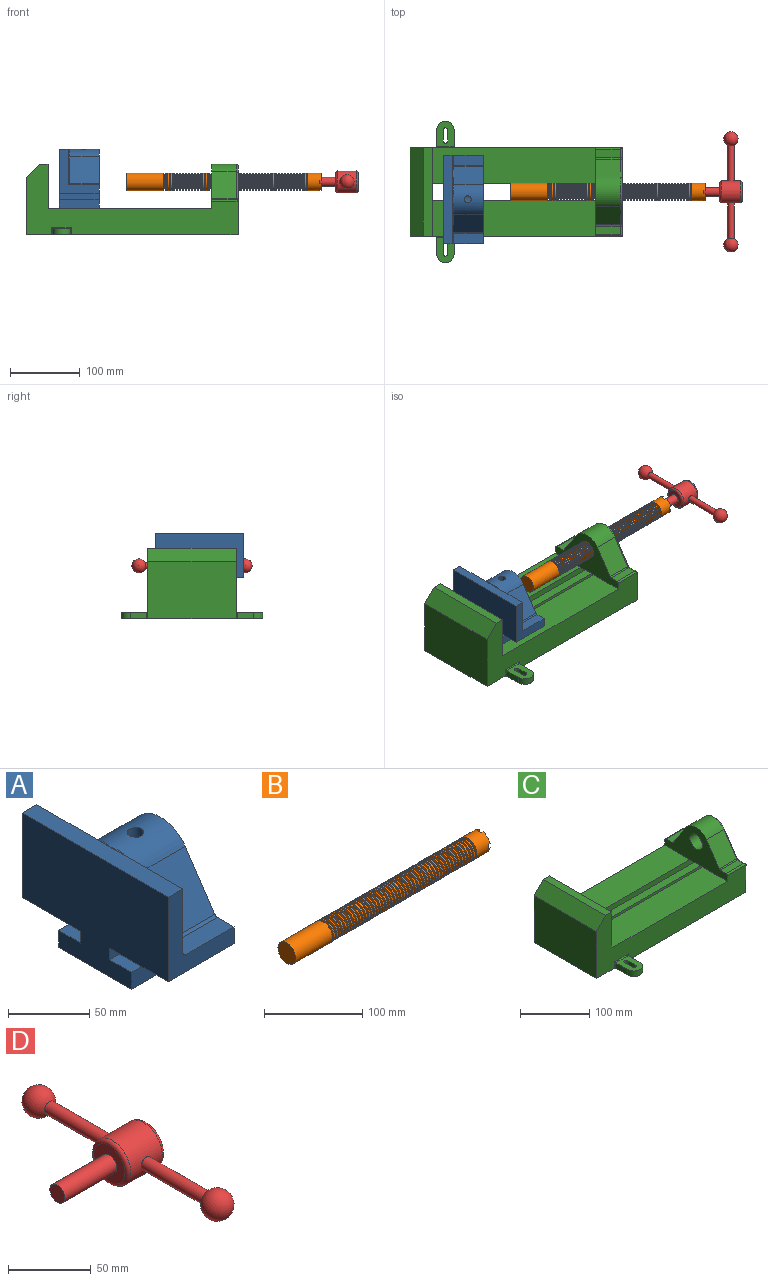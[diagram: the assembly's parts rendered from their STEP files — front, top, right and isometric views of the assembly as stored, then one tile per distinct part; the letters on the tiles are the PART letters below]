
ASSEMBLY  parts=4 mates=3
PART A: 36 faces, bbox 57.2x127x89 mm
  f0: plane 57.15x50.8mm, normal (0,0,-1), area 2903.2mm2, adj f6,f9,f10,f23
  f1: cylinder r=12.7mm len=44.45mm, axis (1,0,0), area 3464.3mm2, adj f6,f15,f16
  f2: plane 41.91x14.52mm, normal (0,0,1), area 608.5mm2, adj f6,f11,f24,f25
  f3: plane 51.86x48.26mm, normal (1,0,0), area 1495.7mm2, adj f8,f10,f31,f33,f35
  f4: plane 51.86x48.26mm, normal (1,0,0), area 1495.7mm2, adj f8,f11,f24,f28,f29
  f5: plane 57.15x50.8mm, normal (0,0,-1), area 2903.2mm2, adj f6,f9,f11,f22
  f6: plane 127x85.09mm, normal (1,0,0), area 5190.6mm2, adj f0,f1,f2,f5,f7,f10,f11,f12
  f7: plane 41.91x14.52mm, normal (0,0,1), area 608.5mm2, adj f6,f10,f30,f31
  f8: plane 127x12.7mm, normal (0,0,1), area 1612.9mm2, adj f3,f4,f9,f10,f11,f26,f34
  f9: plane 127x85.09mm, normal (-1,0,0), area 9096.8mm2, adj f0,f5,f8,f10,f11,f17,f18,f19
  f10: plane 63.5x57.15mm, normal (0,-1,0), area 1372.3mm2, adj f0,f3,f6,f7,f8,f9,f31
  f11: plane 63.5x57.15mm, normal (0,1,0), area 1372.3mm2, adj f2,f4,f5,f6,f8,f9,f24
  f12: plane 41.91x38.43mm, normal (0,-0.83,0.56), area 1939.2mm2, adj f6,f13,f30,f33
  f13: cylinder r=25.4mm len=44.45mm, axis (1,0,0), area 2026.5mm2, adj f6,f12,f14,f16,f26,f28,f34,f35
  f14: plane 41.91x38.43mm, normal (0,0.83,0.56), area 1939.2mm2, adj f6,f13,f25,f29
  f15: plane 25.4x25.4mm, normal (1,0,0), area 506.7mm2, adj f1
  f16: cylinder r=5.08mm len=13.76mm, axis (0,0,1), area 414mm2, adj f1,f13
  f17: plane 57.15x19.05mm, normal (0,0,1), area 1088.7mm2, adj f6,f9,f18,f23
  f18: plane 57.15x12.7mm, normal (0,-1,0), area 725.8mm2, adj f6,f9,f17,f19
  f19: plane 63.5x57.15mm, normal (0,0,-1), area 3629mm2, adj f6,f9,f18,f20
  f20: plane 57.15x12.7mm, normal (0,1,0), area 725.8mm2, adj f6,f9,f19,f21
  f21: plane 57.15x19.05mm, normal (0,0,1), area 1088.7mm2, adj f6,f9,f20,f22
  f22: plane 57.15x8.89mm, normal (0,1,0), area 508.1mm2, adj f5,f6,f9,f21
  f23: plane 57.15x8.89mm, normal (0,-1,0), area 508.1mm2, adj f0,f6,f9,f17
  f24: cylinder r=2.54mm len=14.52mm, axis (0,-1,0), area 57.9mm2, adj f2,f4,f11,f27
  f25: cylinder r=2.54mm len=41.91mm, axis (1,0,0), area 104.3mm2, adj f2,f6,f14,f27
  f26: bspline ~12.24x2.8mm, area 20.9mm2, adj f8,f13,f28
  f27: sphere r=2.54mm, area 6.3mm2, adj f24,f25,f29
  f28: torus R=27.94mm, axis (1,0,0), area 57.8mm2, adj f4,f13,f26,f29
  f29: cylinder r=2.54mm len=39.84mm, axis (0,-0.56,0.83), area 184.6mm2, adj f4,f14,f27,f28
  f30: cylinder r=2.54mm len=41.91mm, axis (1,0,0), area 104.3mm2, adj f6,f7,f12,f32
  f31: cylinder r=2.54mm len=14.52mm, axis (0,-1,0), area 57.9mm2, adj f3,f7,f10,f32
  f32: sphere r=2.54mm, area 6.3mm2, adj f30,f31,f33
  f33: cylinder r=2.54mm len=39.84mm, axis (0,-0.56,-0.83), area 184.6mm2, adj f3,f12,f32,f35
  f34: bspline ~12.24x2.8mm, area 20.9mm2, adj f8,f13,f35
  f35: torus R=27.94mm, axis (1,0,0), area 57.8mm2, adj f3,f13,f33,f34
PART B: 220 faces, bbox 279.4x25.4x25.4 mm
  f0: cylinder r=12.7mm len=25.4mm, axis (-1,0,0), area 1468.2mm2, adj f1,f2,f3,f5,f7,f208,f209,f210
  f1: plane 9.9x9.9mm, normal (1,0,0), area 62.3mm2, adj f0,f4,f213,f216
  f2: plane 9.9x9.9mm, normal (1,0,0), area 62.3mm2, adj f0,f4,f210,f218
  f3: plane 9.9x9.9mm, normal (1,0,0), area 62.3mm2, adj f0,f4,f209,f212
  f4: cylinder r=6.35mm len=25.4mm, axis (1,0,0), area 960.3mm2, adj f1,f2,f3,f5,f6,f208,f209,f210
  f5: plane 9.9x9.9mm, normal (1,0,0), area 62.3mm2, adj f0,f4,f215,f217
  f6: plane 12.7x12.7mm, normal (1,0,0), area 126.7mm2, adj f4
  f7: cone r=12.7mm half-angle=76deg, axis (1,0,0), area 188mm2, adj f0,f9
  f8: cone r=10.16mm half-angle=76deg, axis (-1,0,0), area 188mm2, adj f9,f10
  f9: cylinder r=10.16mm len=20.32mm, axis (1,0,0), area 81.1mm2, adj f7,f8
  f10: cylinder r=12.7mm len=25.4mm, axis (-1,0,0), area 131.7mm2, adj f8,f11
  f11: cone r=12.7mm half-angle=76deg, axis (1,0,0), area 188mm2, adj f10,f13
  f12: cone r=10.16mm half-angle=76deg, axis (-1,0,0), area 188mm2, adj f13,f14
  f13: cylinder r=10.16mm len=20.32mm, axis (1,0,0), area 81.1mm2, adj f11,f12
  f14: cylinder r=12.7mm len=25.4mm, axis (-1,0,0), area 131.7mm2, adj f12,f15
  f15: cone r=12.7mm half-angle=76deg, axis (1,0,0), area 188mm2, adj f14,f17
  f16: cone r=10.16mm half-angle=76deg, axis (-1,0,0), area 188mm2, adj f17,f18
  f17: cylinder r=10.16mm len=20.32mm, axis (1,0,0), area 81.1mm2, adj f15,f16
  f18: cylinder r=12.7mm len=25.4mm, axis (-1,0,0), area 131.7mm2, adj f16,f19
  f19: cone r=12.7mm half-angle=76deg, axis (1,0,0), area 188mm2, adj f18,f21
  f20: cone r=10.16mm half-angle=76deg, axis (-1,0,0), area 188mm2, adj f21,f22
  f21: cylinder r=10.16mm len=20.32mm, axis (1,0,0), area 81.1mm2, adj f19,f20
  f22: cylinder r=12.7mm len=25.4mm, axis (-1,0,0), area 131.7mm2, adj f20,f23
  f23: cone r=12.7mm half-angle=76deg, axis (1,0,0), area 188mm2, adj f22,f25
  f24: cone r=10.16mm half-angle=76deg, axis (-1,0,0), area 188mm2, adj f25,f26
  f25: cylinder r=10.16mm len=20.32mm, axis (1,0,0), area 81.1mm2, adj f23,f24
  f26: cylinder r=12.7mm len=25.4mm, axis (-1,0,0), area 131.7mm2, adj f24,f27
  f27: cone r=12.7mm half-angle=76deg, axis (1,0,0), area 188mm2, adj f26,f29
  f28: cone r=10.16mm half-angle=76deg, axis (-1,0,0), area 188mm2, adj f29,f30
  f29: cylinder r=10.16mm len=20.32mm, axis (1,0,0), area 81.1mm2, adj f27,f28
  f30: cylinder r=12.7mm len=25.4mm, axis (-1,0,0), area 131.7mm2, adj f28,f31
  f31: cone r=12.7mm half-angle=76deg, axis (1,0,0), area 188mm2, adj f30,f33
  f32: cone r=10.16mm half-angle=76deg, axis (-1,0,0), area 188mm2, adj f33,f34
  f33: cylinder r=10.16mm len=20.32mm, axis (1,0,0), area 81.1mm2, adj f31,f32
  f34: cylinder r=12.7mm len=25.4mm, axis (-1,0,0), area 131.7mm2, adj f32,f35
  f35: cone r=12.7mm half-angle=76deg, axis (1,0,0), area 188mm2, adj f34,f37
  f36: cone r=10.16mm half-angle=76deg, axis (-1,0,0), area 188mm2, adj f37,f38
  f37: cylinder r=10.16mm len=20.32mm, axis (1,0,0), area 81.1mm2, adj f35,f36
  f38: cylinder r=12.7mm len=25.4mm, axis (-1,0,0), area 131.7mm2, adj f36,f39
  f39: cone r=12.7mm half-angle=76deg, axis (1,0,0), area 188mm2, adj f38,f41
  f40: cone r=10.16mm half-angle=76deg, axis (-1,0,0), area 188mm2, adj f41,f42
  f41: cylinder r=10.16mm len=20.32mm, axis (1,0,0), area 81.1mm2, adj f39,f40
  f42: cylinder r=12.7mm len=25.4mm, axis (-1,0,0), area 131.7mm2, adj f40,f43
  f43: cone r=12.7mm half-angle=76deg, axis (1,0,0), area 188mm2, adj f42,f45
  f44: cone r=10.16mm half-angle=76deg, axis (-1,0,0), area 188mm2, adj f45,f46
  f45: cylinder r=10.16mm len=20.32mm, axis (1,0,0), area 81.1mm2, adj f43,f44
  f46: cylinder r=12.7mm len=25.4mm, axis (-1,0,0), area 131.7mm2, adj f44,f47
  f47: cone r=12.7mm half-angle=76deg, axis (1,0,0), area 188mm2, adj f46,f49
  f48: cone r=10.16mm half-angle=76deg, axis (-1,0,0), area 188mm2, adj f49,f50
  f49: cylinder r=10.16mm len=20.32mm, axis (1,0,0), area 81.1mm2, adj f47,f48
  f50: cylinder r=12.7mm len=25.4mm, axis (-1,0,0), area 131.7mm2, adj f48,f51
  f51: cone r=12.7mm half-angle=76deg, axis (1,0,0), area 188mm2, adj f50,f53
  f52: cone r=10.16mm half-angle=76deg, axis (-1,0,0), area 188mm2, adj f53,f54
  f53: cylinder r=10.16mm len=20.32mm, axis (1,0,0), area 81.1mm2, adj f51,f52
  f54: cylinder r=12.7mm len=25.4mm, axis (-1,0,0), area 131.7mm2, adj f52,f55
  f55: cone r=12.7mm half-angle=76deg, axis (1,0,0), area 188mm2, adj f54,f57
  f56: cone r=10.16mm half-angle=76deg, axis (-1,0,0), area 188mm2, adj f57,f58
  f57: cylinder r=10.16mm len=20.32mm, axis (1,0,0), area 81.1mm2, adj f55,f56
  f58: cylinder r=12.7mm len=25.4mm, axis (-1,0,0), area 131.7mm2, adj f56,f59
  f59: cone r=12.7mm half-angle=76deg, axis (1,0,0), area 188mm2, adj f58,f61
  f60: cone r=10.16mm half-angle=76deg, axis (-1,0,0), area 188mm2, adj f61,f62
  f61: cylinder r=10.16mm len=20.32mm, axis (1,0,0), area 81.1mm2, adj f59,f60
  f62: cylinder r=12.7mm len=25.4mm, axis (-1,0,0), area 131.7mm2, adj f60,f63
  f63: cone r=12.7mm half-angle=76deg, axis (1,0,0), area 188mm2, adj f62,f65
  f64: cone r=10.16mm half-angle=76deg, axis (-1,0,0), area 188mm2, adj f65,f66
  f65: cylinder r=10.16mm len=20.32mm, axis (1,0,0), area 81.1mm2, adj f63,f64
  f66: cylinder r=12.7mm len=25.4mm, axis (-1,0,0), area 131.7mm2, adj f64,f67
  f67: cone r=12.7mm half-angle=76deg, axis (1,0,0), area 188mm2, adj f66,f69
  f68: cone r=10.16mm half-angle=76deg, axis (-1,0,0), area 188mm2, adj f69,f70
  f69: cylinder r=10.16mm len=20.32mm, axis (1,0,0), area 81.1mm2, adj f67,f68
  f70: cylinder r=12.7mm len=25.4mm, axis (-1,0,0), area 131.7mm2, adj f68,f71
  f71: cone r=12.7mm half-angle=76deg, axis (1,0,0), area 188mm2, adj f70,f73
  f72: cone r=10.16mm half-angle=76deg, axis (-1,0,0), area 188mm2, adj f73,f74
  f73: cylinder r=10.16mm len=20.32mm, axis (1,0,0), area 81.1mm2, adj f71,f72
  f74: cylinder r=12.7mm len=25.4mm, axis (-1,0,0), area 131.7mm2, adj f72,f75
  f75: cone r=12.7mm half-angle=76deg, axis (1,0,0), area 188mm2, adj f74,f77
  f76: cone r=10.16mm half-angle=76deg, axis (-1,0,0), area 188mm2, adj f77,f78
  f77: cylinder r=10.16mm len=20.32mm, axis (1,0,0), area 81.1mm2, adj f75,f76
  f78: cylinder r=12.7mm len=25.4mm, axis (-1,0,0), area 131.7mm2, adj f76,f79
  f79: cone r=12.7mm half-angle=76deg, axis (1,0,0), area 188mm2, adj f78,f81
  f80: cone r=10.16mm half-angle=76deg, axis (-1,0,0), area 188mm2, adj f81,f82
  f81: cylinder r=10.16mm len=20.32mm, axis (1,0,0), area 81.1mm2, adj f79,f80
  f82: cylinder r=12.7mm len=25.4mm, axis (-1,0,0), area 131.7mm2, adj f80,f83
  f83: cone r=12.7mm half-angle=76deg, axis (1,0,0), area 188mm2, adj f82,f85
  f84: cone r=10.16mm half-angle=76deg, axis (-1,0,0), area 188mm2, adj f85,f86
  f85: cylinder r=10.16mm len=20.32mm, axis (1,0,0), area 81.1mm2, adj f83,f84
  f86: cylinder r=12.7mm len=25.4mm, axis (-1,0,0), area 131.7mm2, adj f84,f87
  f87: cone r=12.7mm half-angle=76deg, axis (1,0,0), area 188mm2, adj f86,f89
  f88: cone r=10.16mm half-angle=76deg, axis (-1,0,0), area 188mm2, adj f89,f90
  f89: cylinder r=10.16mm len=20.32mm, axis (1,0,0), area 81.1mm2, adj f87,f88
  f90: cylinder r=12.7mm len=25.4mm, axis (-1,0,0), area 131.7mm2, adj f88,f91
  f91: cone r=12.7mm half-angle=76deg, axis (1,0,0), area 188mm2, adj f90,f93
  f92: cone r=10.16mm half-angle=76deg, axis (-1,0,0), area 188mm2, adj f93,f94
  f93: cylinder r=10.16mm len=20.32mm, axis (1,0,0), area 81.1mm2, adj f91,f92
  f94: cylinder r=12.7mm len=25.4mm, axis (-1,0,0), area 131.7mm2, adj f92,f95
  f95: cone r=12.7mm half-angle=76deg, axis (1,0,0), area 188mm2, adj f94,f97
  f96: cone r=10.16mm half-angle=76deg, axis (-1,0,0), area 188mm2, adj f97,f98
  f97: cylinder r=10.16mm len=20.32mm, axis (1,0,0), area 81.1mm2, adj f95,f96
  f98: cylinder r=12.7mm len=25.4mm, axis (-1,0,0), area 131.7mm2, adj f96,f99
  f99: cone r=12.7mm half-angle=76deg, axis (1,0,0), area 188mm2, adj f98,f101
  f100: cone r=10.16mm half-angle=76deg, axis (-1,0,0), area 188mm2, adj f101,f102
  f101: cylinder r=10.16mm len=20.32mm, axis (1,0,0), area 81.1mm2, adj f99,f100
  f102: cylinder r=12.7mm len=25.4mm, axis (-1,0,0), area 131.7mm2, adj f100,f103
  f103: cone r=12.7mm half-angle=76deg, axis (1,0,0), area 188mm2, adj f102,f105
  f104: cone r=10.16mm half-angle=76deg, axis (-1,0,0), area 188mm2, adj f105,f106
  f105: cylinder r=10.16mm len=20.32mm, axis (1,0,0), area 81.1mm2, adj f103,f104
  f106: cylinder r=12.7mm len=25.4mm, axis (-1,0,0), area 131.7mm2, adj f104,f107
  f107: cone r=12.7mm half-angle=76deg, axis (1,0,0), area 188mm2, adj f106,f109
  f108: cone r=10.16mm half-angle=76deg, axis (-1,0,0), area 188mm2, adj f109,f110
  f109: cylinder r=10.16mm len=20.32mm, axis (1,0,0), area 81.1mm2, adj f107,f108
  f110: cylinder r=12.7mm len=25.4mm, axis (-1,0,0), area 131.7mm2, adj f108,f111
  f111: cone r=12.7mm half-angle=76deg, axis (1,0,0), area 188mm2, adj f110,f113
  f112: cone r=10.16mm half-angle=76deg, axis (-1,0,0), area 188mm2, adj f113,f114
  f113: cylinder r=10.16mm len=20.32mm, axis (1,0,0), area 81.1mm2, adj f111,f112
  f114: cylinder r=12.7mm len=25.4mm, axis (-1,0,0), area 131.7mm2, adj f112,f115
  f115: cone r=12.7mm half-angle=76deg, axis (1,0,0), area 188mm2, adj f114,f117
  f116: cone r=10.16mm half-angle=76deg, axis (-1,0,0), area 188mm2, adj f117,f118
  f117: cylinder r=10.16mm len=20.32mm, axis (1,0,0), area 81.1mm2, adj f115,f116
  f118: cylinder r=12.7mm len=25.4mm, axis (-1,0,0), area 131.7mm2, adj f116,f119
  f119: cone r=12.7mm half-angle=76deg, axis (1,0,0), area 188mm2, adj f118,f121
  f120: cone r=10.16mm half-angle=76deg, axis (-1,0,0), area 188mm2, adj f121,f122
  f121: cylinder r=10.16mm len=20.32mm, axis (1,0,0), area 81.1mm2, adj f119,f120
  f122: cylinder r=12.7mm len=25.4mm, axis (-1,0,0), area 131.7mm2, adj f120,f123
  f123: cone r=12.7mm half-angle=76deg, axis (1,0,0), area 188mm2, adj f122,f125
  f124: cone r=10.16mm half-angle=76deg, axis (-1,0,0), area 188mm2, adj f125,f126
  f125: cylinder r=10.16mm len=20.32mm, axis (1,0,0), area 81.1mm2, adj f123,f124
  f126: cylinder r=12.7mm len=25.4mm, axis (-1,0,0), area 131.7mm2, adj f124,f127
  f127: cone r=12.7mm half-angle=76deg, axis (1,0,0), area 188mm2, adj f126,f129
  f128: cone r=10.16mm half-angle=76deg, axis (-1,0,0), area 188mm2, adj f129,f130
  f129: cylinder r=10.16mm len=20.32mm, axis (1,0,0), area 81.1mm2, adj f127,f128
  f130: cylinder r=12.7mm len=25.4mm, axis (-1,0,0), area 131.7mm2, adj f128,f131
  f131: cone r=12.7mm half-angle=76deg, axis (1,0,0), area 188mm2, adj f130,f133
  f132: cone r=10.16mm half-angle=76deg, axis (-1,0,0), area 188mm2, adj f133,f134
  f133: cylinder r=10.16mm len=20.32mm, axis (1,0,0), area 81.1mm2, adj f131,f132
  f134: cylinder r=12.7mm len=25.4mm, axis (-1,0,0), area 131.7mm2, adj f132,f135
  f135: cone r=12.7mm half-angle=76deg, axis (1,0,0), area 188mm2, adj f134,f137
  f136: cone r=10.16mm half-angle=76deg, axis (-1,0,0), area 188mm2, adj f137,f138
  f137: cylinder r=10.16mm len=20.32mm, axis (1,0,0), area 81.1mm2, adj f135,f136
  f138: cylinder r=12.7mm len=25.4mm, axis (-1,0,0), area 131.7mm2, adj f136,f139
  f139: cone r=12.7mm half-angle=76deg, axis (1,0,0), area 188mm2, adj f138,f141
  f140: cone r=10.16mm half-angle=76deg, axis (-1,0,0), area 188mm2, adj f141,f142
  f141: cylinder r=10.16mm len=20.32mm, axis (1,0,0), area 81.1mm2, adj f139,f140
  f142: cylinder r=12.7mm len=25.4mm, axis (-1,0,0), area 131.7mm2, adj f140,f143
  f143: cone r=12.7mm half-angle=76deg, axis (1,0,0), area 188mm2, adj f142,f145
  f144: cone r=10.16mm half-angle=76deg, axis (-1,0,0), area 188mm2, adj f145,f146
  f145: cylinder r=10.16mm len=20.32mm, axis (1,0,0), area 81.1mm2, adj f143,f144
  f146: cylinder r=12.7mm len=25.4mm, axis (-1,0,0), area 131.7mm2, adj f144,f147
  f147: cone r=12.7mm half-angle=76deg, axis (1,0,0), area 188mm2, adj f146,f149
  f148: cone r=10.16mm half-angle=76deg, axis (-1,0,0), area 188mm2, adj f149,f150
  f149: cylinder r=10.16mm len=20.32mm, axis (1,0,0), area 81.1mm2, adj f147,f148
  f150: cylinder r=12.7mm len=25.4mm, axis (-1,0,0), area 131.7mm2, adj f148,f151
  f151: cone r=12.7mm half-angle=76deg, axis (1,0,0), area 188mm2, adj f150,f153
  f152: cone r=10.16mm half-angle=76deg, axis (-1,0,0), area 188mm2, adj f153,f154
  f153: cylinder r=10.16mm len=20.32mm, axis (1,0,0), area 81.1mm2, adj f151,f152
  f154: cylinder r=12.7mm len=25.4mm, axis (-1,0,0), area 131.7mm2, adj f152,f155
  f155: cone r=12.7mm half-angle=76deg, axis (1,0,0), area 188mm2, adj f154,f157
  f156: cone r=10.16mm half-angle=76deg, axis (-1,0,0), area 188mm2, adj f157,f158
  f157: cylinder r=10.16mm len=20.32mm, axis (1,0,0), area 81.1mm2, adj f155,f156
  f158: cylinder r=12.7mm len=25.4mm, axis (-1,0,0), area 131.7mm2, adj f156,f159
  f159: cone r=12.7mm half-angle=76deg, axis (1,0,0), area 188mm2, adj f158,f161
  f160: cone r=10.16mm half-angle=76deg, axis (-1,0,0), area 188mm2, adj f161,f162
  f161: cylinder r=10.16mm len=20.32mm, axis (1,0,0), area 81.1mm2, adj f159,f160
  f162: cylinder r=12.7mm len=25.4mm, axis (-1,0,0), area 131.7mm2, adj f160,f163
  f163: cone r=12.7mm half-angle=76deg, axis (1,0,0), area 188mm2, adj f162,f165
  f164: cone r=10.16mm half-angle=76deg, axis (-1,0,0), area 188mm2, adj f165,f166
  f165: cylinder r=10.16mm len=20.32mm, axis (1,0,0), area 81.1mm2, adj f163,f164
  f166: cylinder r=12.7mm len=25.4mm, axis (-1,0,0), area 131.7mm2, adj f164,f167
  f167: cone r=12.7mm half-angle=76deg, axis (1,0,0), area 188mm2, adj f166,f169
  f168: cone r=10.16mm half-angle=76deg, axis (-1,0,0), area 188mm2, adj f169,f170
  f169: cylinder r=10.16mm len=20.32mm, axis (1,0,0), area 81.1mm2, adj f167,f168
  f170: cylinder r=12.7mm len=25.4mm, axis (-1,0,0), area 131.7mm2, adj f168,f171
  f171: cone r=12.7mm half-angle=76deg, axis (1,0,0), area 188mm2, adj f170,f173
  f172: cone r=10.16mm half-angle=76deg, axis (-1,0,0), area 188mm2, adj f173,f174
  f173: cylinder r=10.16mm len=20.32mm, axis (1,0,0), area 81.1mm2, adj f171,f172
  f174: cylinder r=12.7mm len=25.4mm, axis (-1,0,0), area 131.7mm2, adj f172,f175
  f175: cone r=12.7mm half-angle=76deg, axis (1,0,0), area 188mm2, adj f174,f177
  f176: cone r=10.16mm half-angle=76deg, axis (-1,0,0), area 188mm2, adj f177,f178
  f177: cylinder r=10.16mm len=20.32mm, axis (1,0,0), area 81.1mm2, adj f175,f176
  f178: cylinder r=12.7mm len=25.4mm, axis (-1,0,0), area 131.7mm2, adj f176,f179
  f179: cone r=12.7mm half-angle=76deg, axis (1,0,0), area 188mm2, adj f178,f181
  f180: cone r=10.16mm half-angle=76deg, axis (-1,0,0), area 188mm2, adj f181,f182
  f181: cylinder r=10.16mm len=20.32mm, axis (1,0,0), area 81.1mm2, adj f179,f180
  f182: cylinder r=12.7mm len=25.4mm, axis (-1,0,0), area 131.7mm2, adj f180,f183
  f183: cone r=12.7mm half-angle=76deg, axis (1,0,0), area 188mm2, adj f182,f185
  f184: cone r=10.16mm half-angle=76deg, axis (-1,0,0), area 188mm2, adj f185,f186
  f185: cylinder r=10.16mm len=20.32mm, axis (1,0,0), area 81.1mm2, adj f183,f184
  f186: cylinder r=12.7mm len=25.4mm, axis (-1,0,0), area 131.7mm2, adj f184,f187
  f187: cone r=12.7mm half-angle=76deg, axis (1,0,0), area 188mm2, adj f186,f189
  f188: cone r=10.16mm half-angle=76deg, axis (-1,0,0), area 188mm2, adj f189,f190
  f189: cylinder r=10.16mm len=20.32mm, axis (1,0,0), area 81.1mm2, adj f187,f188
  f190: cylinder r=12.7mm len=25.4mm, axis (-1,0,0), area 131.7mm2, adj f188,f191
  f191: cone r=12.7mm half-angle=76deg, axis (1,0,0), area 188mm2, adj f190,f193
  f192: cone r=10.16mm half-angle=76deg, axis (-1,0,0), area 188mm2, adj f193,f194
  f193: cylinder r=10.16mm len=20.32mm, axis (1,0,0), area 81.1mm2, adj f191,f192
  f194: cylinder r=12.7mm len=25.4mm, axis (-1,0,0), area 131.7mm2, adj f192,f195
  f195: cone r=12.7mm half-angle=76deg, axis (1,0,0), area 188mm2, adj f194,f197
  f196: cone r=10.16mm half-angle=76deg, axis (-1,0,0), area 188mm2, adj f197,f198
  f197: cylinder r=10.16mm len=20.32mm, axis (1,0,0), area 81.1mm2, adj f195,f196
  f198: cylinder r=12.7mm len=25.4mm, axis (-1,0,0), area 131.7mm2, adj f196,f199
  f199: cone r=12.7mm half-angle=76deg, axis (1,0,0), area 188mm2, adj f198,f201
  f200: cone r=10.16mm half-angle=76deg, axis (-1,0,0), area 188mm2, adj f201,f202
  f201: cylinder r=10.16mm len=20.32mm, axis (1,0,0), area 81.1mm2, adj f199,f200
  f202: cylinder r=12.7mm len=25.4mm, axis (-1,0,0), area 131.7mm2, adj f200,f203
  f203: cone r=12.7mm half-angle=76deg, axis (1,0,0), area 188mm2, adj f202,f205
  f204: cone r=10.16mm half-angle=76deg, axis (-1,0,0), area 188mm2, adj f205,f207
  f205: cylinder r=10.16mm len=20.32mm, axis (1,0,0), area 81.1mm2, adj f203,f204
  f206: plane 25.4x25.4mm, normal (-1,0,0), area 506.7mm2, adj f207
  f207: cylinder r=12.7mm len=52.45mm, axis (-1,0,0), area 4185.4mm2, adj f204,f206
  f208: plane 6.88x5.08mm, normal (1,0,0), area 32.7mm2, adj f0,f4,f209,f210
  f209: plane 6.62x2.54mm, normal (0,-1,0), area 16.8mm2, adj f0,f3,f4,f208
  f210: plane 6.62x2.54mm, normal (0,1,0), area 16.8mm2, adj f0,f2,f4,f208
  f211: plane 6.88x5.08mm, normal (1,0,0), area 32.7mm2, adj f0,f4,f212,f213
  f212: plane 6.62x2.54mm, normal (0,0,1), area 16.8mm2, adj f0,f3,f4,f211
  f213: plane 6.62x2.54mm, normal (0,0,-1), area 16.8mm2, adj f0,f1,f4,f211
  f214: plane 6.88x5.08mm, normal (1,0,0), area 32.7mm2, adj f0,f4,f215,f216
  f215: plane 6.62x2.54mm, normal (0,1,0), area 16.8mm2, adj f0,f4,f5,f214
  f216: plane 6.62x2.54mm, normal (0,-1,0), area 16.8mm2, adj f0,f1,f4,f214
  f217: plane 6.62x2.54mm, normal (0,0,-1), area 16.8mm2, adj f0,f4,f5,f219
  f218: plane 6.62x2.54mm, normal (0,0,1), area 16.8mm2, adj f0,f2,f4,f219
  f219: plane 6.88x5.08mm, normal (1,0,0), area 32.7mm2, adj f0,f4,f217,f218
PART C: 61 faces, bbox 304.8x203.2x103.7 mm
  f0: plane 304.8x101.6mm, normal (0,1,0), area 13520.3mm2, adj f3,f4,f5,f6,f7,f8,f9,f16
  f1: plane 304.8x101.6mm, normal (0,-1,0), area 13520.3mm2, adj f2,f3,f5,f6,f7,f8,f9,f16
  f2: plane 234.95x50.8mm, normal (0,0,1), area 11935.5mm2, adj f1,f5,f16,f26
  f3: plane 127x99.06mm, normal (1,0,0), area 7097.5mm2, adj f0,f1,f9,f14,f17,f18,f19,f20
  f4: plane 234.95x50.8mm, normal (0,0,1), area 11935.5mm2, adj f0,f5,f16,f27
  f5: plane 127x101.6mm, normal (1,0,0), area 9516.1mm2, adj f0,f1,f2,f4,f6,f9,f18,f19
  f6: plane 127x12.7mm, normal (0,0,1), area 1612.9mm2, adj f0,f1,f5,f7
  f7: plane 127x19.05mm, normal (-0.71,0,0.71), area 3421.5mm2, adj f0,f1,f6,f8
  f8: plane 127x82.55mm, normal (-1,0,0), area 10483.8mm2, adj f0,f1,f7,f9
  f9: plane 304.8x203.2mm, normal (0,0,-1), area 33298.3mm2, adj f0,f1,f3,f5,f8,f21,f22,f39
  f10: plane 35.56x11.98mm, normal (0,0,1), area 426mm2, adj f16,f28,f29,f30
  f11: plane 38.43x35.56mm, normal (0,0.83,0.56), area 1645.4mm2, adj f12,f16,f29,f32
  f12: cylinder r=25.4mm len=42.19mm, axis (1,0,0), area 1770.2mm2, adj f11,f13,f16,f33
  f13: plane 38.43x35.56mm, normal (0,-0.83,0.56), area 1645.4mm2, adj f12,f16,f34,f35
  f14: cylinder r=12.7mm len=38.1mm, axis (1,0,0), area 3040.2mm2, adj f3,f16
  f15: plane 35.56x11.98mm, normal (0,0,1), area 426mm2, adj f16,f34,f36,f38
  f16: plane 127x63.5mm, normal (-1,0,0), area 4155.5mm2, adj f0,f1,f2,f4,f10,f11,f12,f13
  f17: plane 38.1x25.4mm, normal (0,0,-1), area 967.7mm2, adj f3,f16,f26,f27
  f18: plane 273.05x19.05mm, normal (0,0,-1), area 5201.6mm2, adj f3,f5,f19,f26
  f19: plane 273.05x12.7mm, normal (0,1,0), area 3467.7mm2, adj f3,f5,f18,f20
  f20: plane 273.05x19.05mm, normal (0,0,1), area 5201.6mm2, adj f3,f5,f19,f21
  f21: plane 273.05x16.51mm, normal (0,1,0), area 4508.1mm2, adj f3,f5,f9,f20
  f22: plane 273.05x16.51mm, normal (0,-1,0), area 4508.1mm2, adj f3,f5,f9,f23
  f23: plane 273.05x19.05mm, normal (0,0,1), area 5201.6mm2, adj f3,f5,f22,f24
  f24: plane 273.05x12.7mm, normal (0,-1,0), area 3467.7mm2, adj f3,f5,f23,f25
  f25: plane 273.05x19.05mm, normal (0,0,-1), area 5201.6mm2, adj f3,f5,f24,f27
  f26: plane 273.05x8.89mm, normal (0,1,0), area 2427.4mm2, adj f2,f3,f5,f17,f18
  f27: plane 273.05x8.89mm, normal (0,-1,0), area 2427.4mm2, adj f3,f4,f5,f17,f25
  f28: cylinder r=2.54mm len=38.1mm, axis (1,0,0), area 148.3mm2, adj f0,f10,f16,f30
  f29: cylinder r=2.54mm len=35.56mm, axis (-1,0,0), area 88.5mm2, adj f10,f11,f16,f31
  f30: cylinder r=2.54mm len=14.52mm, axis (0,1,0), area 54.3mm2, adj f3,f10,f28,f31
  f31: torus R=5.08mm, axis (-1,0,0), area 13.5mm2, adj f3,f29,f30,f32
  f32: cylinder r=2.54mm len=39.84mm, axis (0,0.56,-0.83), area 184.6mm2, adj f3,f11,f31,f33
  f33: torus R=22.86mm, axis (-1,0,0), area 191.4mm2, adj f3,f12,f32,f35
  f34: cylinder r=2.54mm len=35.56mm, axis (-1,0,0), area 88.5mm2, adj f13,f15,f16,f37
  f35: cylinder r=2.54mm len=39.84mm, axis (0,0.56,0.83), area 184.6mm2, adj f3,f13,f33,f37
  f36: cylinder r=2.54mm len=38.1mm, axis (-1,0,0), area 148.3mm2, adj f1,f15,f16,f38
  f37: torus R=5.08mm, axis (-1,0,0), area 13.5mm2, adj f3,f34,f35,f38
  f38: cylinder r=2.54mm len=14.52mm, axis (0,1,0), area 54.3mm2, adj f3,f15,f36,f37
  f39: plane 23.88x9.53mm, normal (-1,0,0), area 227.4mm2, adj f9,f45,f46,f60
  f40: plane 23.88x9.53mm, normal (1,0,0), area 227.4mm2, adj f9,f45,f46,f58
  f41: cylinder r=3.3mm len=9.53mm, axis (0,0,-1), area 98.8mm2, adj f9,f42,f44,f46
  f42: plane 15.62x9.53mm, normal (-1,0,0), area 148.8mm2, adj f9,f41,f43,f46
  f43: cylinder r=3.3mm len=9.53mm, axis (0,0,-1), area 98.8mm2, adj f9,f42,f44,f46
  f44: plane 15.62x9.53mm, normal (1,0,0), area 148.8mm2, adj f9,f41,f43,f46
  f45: cylinder r=12.7mm len=25.4mm, axis (0,0,-1), area 380mm2, adj f9,f39,f40,f46
  f46: plane 36.58x25.4mm, normal (0,0,1), area 722.4mm2, adj f39,f40,f41,f42,f43,f44,f45,f59
  f47: plane 23.88x9.53mm, normal (-1,0,0), area 227.4mm2, adj f9,f53,f54,f56
  f48: plane 23.88x9.53mm, normal (1,0,0), area 227.4mm2, adj f9,f53,f54,f55
  f49: cylinder r=3.3mm len=9.53mm, axis (0,0,-1), area 98.8mm2, adj f9,f50,f52,f54
  f50: plane 15.62x9.53mm, normal (-1,0,0), area 148.8mm2, adj f9,f49,f51,f54
  f51: cylinder r=3.3mm len=9.53mm, axis (0,0,-1), area 98.8mm2, adj f9,f50,f52,f54
  f52: plane 15.62x9.53mm, normal (1,0,0), area 148.8mm2, adj f9,f49,f51,f54
  f53: cylinder r=12.7mm len=25.4mm, axis (0,0,-1), area 380mm2, adj f9,f47,f48,f54
  f54: plane 36.58x25.4mm, normal (0,0,1), area 722.4mm2, adj f47,f48,f49,f50,f51,f52,f53,f57
  f55: cylinder r=1.52mm len=11.05mm, axis (0,0,-1), area 24.1mm2, adj f0,f9,f48,f57
  f56: cylinder r=1.52mm len=11.05mm, axis (0,0,1), area 24.1mm2, adj f0,f9,f47,f57
  f57: cylinder r=1.52mm len=28.45mm, axis (1,0,0), area 63.5mm2, adj f0,f54,f55,f56
  f58: cylinder r=1.52mm len=11.05mm, axis (0,0,1), area 24.1mm2, adj f1,f9,f40,f59
  f59: cylinder r=1.52mm len=28.45mm, axis (-1,0,0), area 63.5mm2, adj f1,f46,f58,f60
  f60: cylinder r=1.52mm len=11.05mm, axis (0,0,-1), area 24.1mm2, adj f1,f9,f39,f59
PART D: 11 faces, bbox 76.2x172.7x34.4 mm
  f0: sphere r=10.16mm, area 1231.8mm2, adj f1
  f1: cylinder r=4.45mm len=51.82mm, axis (0,1,0), area 1438.5mm2, adj f0,f4
  f2: sphere r=10.16mm, area 1231.8mm2, adj f3
  f3: cylinder r=4.45mm len=51.82mm, axis (0,1,0), area 1438.5mm2, adj f2,f4
  f4: cylinder r=15.88mm len=31.75mm, axis (-1,0,0), area 2534.7mm2, adj f1,f3,f9,f10
  f5: cylinder r=6.35mm len=44.45mm, axis (-1,0,0), area 1773.5mm2, adj f6,f8
  f6: plane 12.7x12.7mm, normal (-1,0,0), area 126.7mm2, adj f5
  f7: plane 26.67x26.67mm, normal (1,0,0), area 558.6mm2, adj f10
  f8: plane 26.67x26.67mm, normal (-1,0,0), area 432mm2, adj f5,f9
  f9: torus R=13.33mm, axis (1,0,0), area 374.8mm2, adj f4,f8
  f10: torus R=13.33mm, axis (1,0,0), area 374.8mm2, adj f4,f7
PLACE A t=(-57.68,-13.27,6.5)mm
PLACE B t=(26.59,-2.45,-15.09)mm
PLACE C t=(-73.85,-2.45,-15.09)mm
PLACE D t=(28.75,-2.45,-15.09)mm
MATE planar C.f2 <-> A.f19  axis (0,0,1) through (-229.42,-40.55,23.01)mm
MATE cylindrical B.f7 <-> C.f12  axis (-1,0,0) through (-233.76,-2.45,61.11)mm
MATE fastened D.f5 <-> B.f4  axis (-1,0,0) through (22.4,-2.45,61.11)mm
